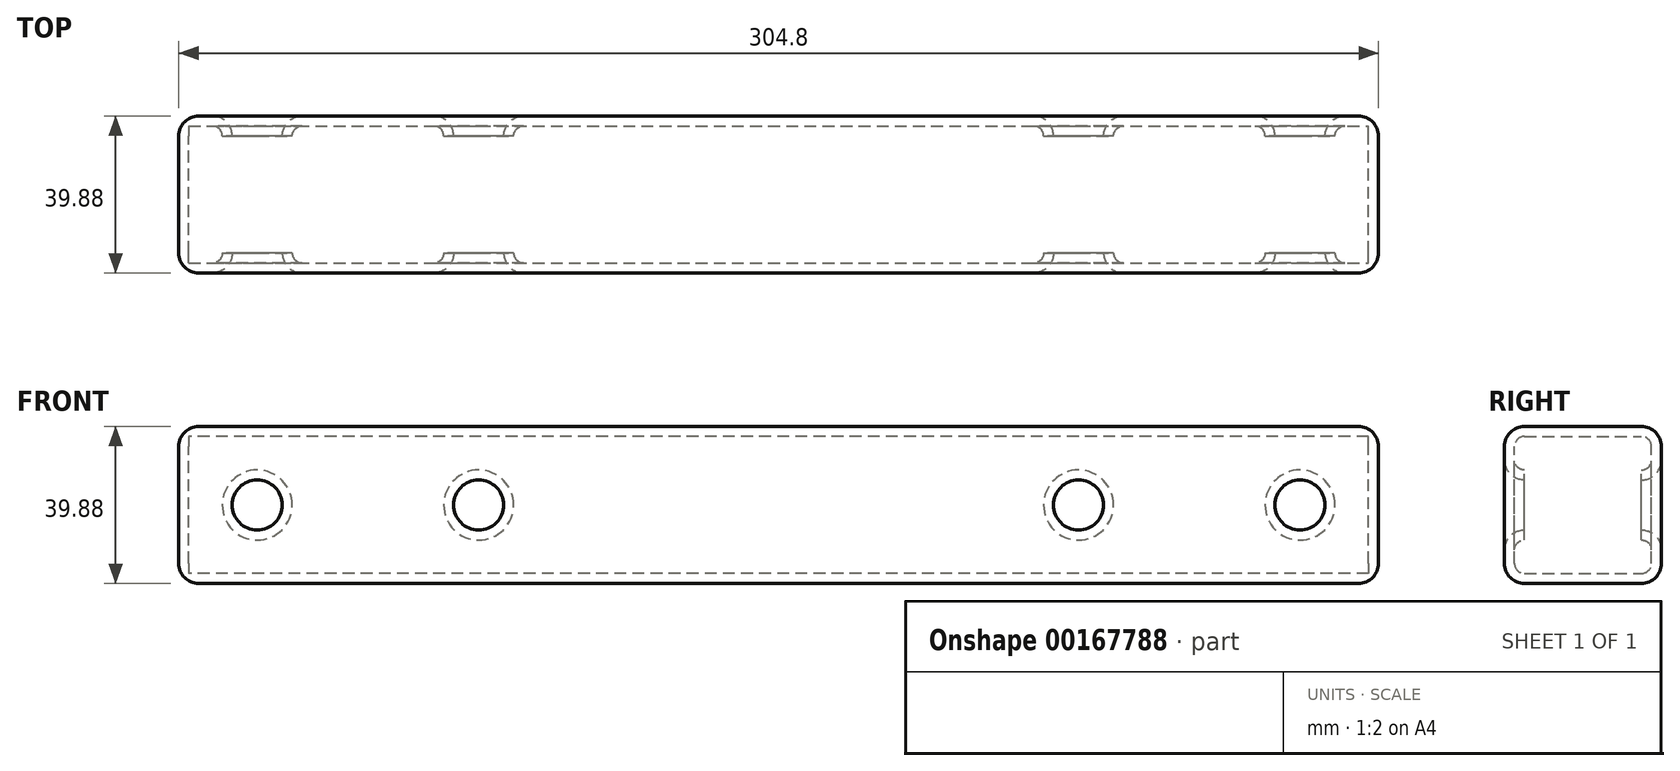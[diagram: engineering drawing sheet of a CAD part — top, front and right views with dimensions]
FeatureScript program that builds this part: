
annotation { "Feature Type Name" : "Feature", "Feature Type Description" : "" }
export const myFeature = defineFeature(function(context is Context, id is Id, definition is map)
    precondition{}
    {
        {
            var Q0;
            Q0=qCreatedBy(makeId("Front.planeOp"),FACE);
            var sketch = newSketch(context, id + "F0", { "sketchPlane" : qUnion([Q0])});
            skLineSegment(sketch, "E0.bottom", {"start": v(152.4, -19.94) * mm, "end": v(-152.4, -19.94) * mm});
            skLineSegment(sketch, "E0.top", {"start": v(152.4, 19.94) * mm, "end": v(-152.4, 19.94) * mm});
            skLineSegment(sketch, "E0.left", {"start": v(152.4, -19.94) * mm, "end": v(152.4, 19.94) * mm});
            skLineSegment(sketch, "E0.right", {"start": v(-152.4, -19.94) * mm, "end": v(-152.4, 19.94) * mm});
            skPoint(sketch, "E0.middle", {"position": v(0, 0) * mm});
            skLineSegment(sketch, "E1", {"start": v(-152.4, 19.94) * mm, "end": v(-112.52, 19.94) * mm});
            skLineSegment(sketch, "E2", {"start": v(-112.52, -19.94) * mm, "end": v(-152.4, -19.94) * mm});
            skPoint(sketch, "E3.startSnap0", {"position": v(-132.46, 19.94) * mm});
            skCircle(sketch, "E4", {"center": v(-132.46, 0) * mm, "radius": 6.35 * mm});
            skCircle(sketch, "E5.MirrorC", {"center": v(132.46, 0) * mm, "radius": 6.35 * mm});
            skLineSegment(sketch, "E6", {"start": v(0, 19.94) * mm, "end": v(-76.2, 19.94) * mm});
            skLineSegment(sketch, "E7", {"start": v(0, 19.94) * mm, "end": v(76.2, 19.94) * mm});
            skCircle(sketch, "E8", {"center": v(-76.2, 0) * mm, "radius": 6.35 * mm});
            skCircle(sketch, "E9.MirrorC", {"center": v(76.2, 0) * mm, "radius": 6.35 * mm});
            skSolve(sketch);
        }
        {
            var Q0;
            Q0=qSketchRegion(id+"F0",true);
            extrude(context, id + "F1", {"entities" : qUnion([Q0]), "depth" : 39.88 * mm});
        }
        {
            var Q0;
            Q0=makeQuery(id+"F1.opExtrude","CAP_EDGE",EDGE,{"disambiguationData":[OSD([sQuery(id+"F0.wireOp",EDGE,"E4")])],"isStart":false});
            var Q1;
            Q1=makeQuery(id+"F1.opExtrude","CAP_EDGE",EDGE,{"disambiguationData":[OSD([sQuery(id+"F0.wireOp",EDGE,"E8")])],"isStart":false});
            var Q2;
            Q2=makeQuery(id+"F1.opExtrude","CAP_EDGE",EDGE,{"disambiguationData":[OSD([sQuery(id+"F0.wireOp",EDGE,"E9.MirrorC")])],"isStart":false});
            fillet(context, id + "F2", {"entities" : qUnion([Q0, Q1, Q2]), "radius" : 5.08 * mm, "tangentPropagation" : true, "allowEdgeOverflow" : false});
        }
        {
            var Q0;
            Q0=makeQuery(id+"F1.opExtrude","CAP_EDGE",EDGE,{"disambiguationData":[OSD([sQuery(id+"F0.wireOp",EDGE,"E5.MirrorC")])],"isStart":false});
            var Q1;
            Q1=makeQuery(id+"F1.opExtrude","CAP_EDGE",EDGE,{"disambiguationData":[OSD([sQuery(id+"F0.wireOp",EDGE,"E5.MirrorC")])],"isStart":true});
            var Q2;
            Q2=makeQuery(id+"F1.opExtrude","CAP_EDGE",EDGE,{"disambiguationData":[OSD([sQuery(id+"F0.wireOp",EDGE,"E9.MirrorC")])],"isStart":true});
            var Q3;
            Q3=makeQuery(id+"F1.opExtrude","CAP_EDGE",EDGE,{"disambiguationData":[OSD([sQuery(id+"F0.wireOp",EDGE,"E8")])],"isStart":true});
            var Q4;
            Q4=makeQuery(id+"F1.opExtrude","CAP_EDGE",EDGE,{"disambiguationData":[OSD([sQuery(id+"F0.wireOp",EDGE,"E4")])],"isStart":true});
            var Q5;
            Q5=makeQuery(id+"F1.opExtrude","CAP_EDGE",EDGE,{"disambiguationData":[OSD([sQuery(id+"F0.wireOp",EDGE,"E0.bottom"),sQuery(id+"F0.wireOp",EDGE,"E2")])],"isStart":true});
            var Q6;
            Q6=makeQuery(id+"F1.opExtrude","CAP_EDGE",EDGE,{"disambiguationData":[OSD([sQuery(id+"F0.wireOp",EDGE,"E0.top"),sQuery(id+"F0.wireOp",EDGE,"E1"),sQuery(id+"F0.wireOp",EDGE,"E6"),sQuery(id+"F0.wireOp",EDGE,"E7")])],"isStart":true});
            var Q7;
            Q7=makeQuery(id+"F1.opExtrude","CAP_EDGE",EDGE,{"disambiguationData":[OSD([sQuery(id+"F0.wireOp",EDGE,"E0.top"),sQuery(id+"F0.wireOp",EDGE,"E1"),sQuery(id+"F0.wireOp",EDGE,"E6"),sQuery(id+"F0.wireOp",EDGE,"E7")])],"isStart":false});
            var Q8;
            Q8=makeQuery(id+"F1.opExtrude","CAP_EDGE",EDGE,{"disambiguationData":[OSD([sQuery(id+"F0.wireOp",EDGE,"E0.bottom"),sQuery(id+"F0.wireOp",EDGE,"E2")])],"isStart":false});
            fillet(context, id + "F3", {"entities" : qUnion([Q0, Q1, Q2, Q3, Q4, Q5, Q6, Q7, Q8]), "radius" : 5.08 * mm, "tangentPropagation" : true, "allowEdgeOverflow" : false});
        }
        {
            var Q0;
            Q0=makeQuery(id+"F1.opExtrude","SWEPT_FACE",FACE,{"disambiguationData":[OSD([sQuery(id+"F0.wireOp",EDGE,"E9.MirrorC")])]});
            var Q1;
            Q1=makeQuery(id+"F1.opExtrude","SWEPT_FACE",FACE,{"disambiguationData":[OSD([sQuery(id+"F0.wireOp",EDGE,"E5.MirrorC")])]});
            var Q2;
            Q2=makeQuery(id+"F1.opExtrude","SWEPT_FACE",FACE,{"disambiguationData":[OSD([sQuery(id+"F0.wireOp",EDGE,"E8")])]});
            var Q3;
            Q3=makeQuery(id+"F1.opExtrude","SWEPT_FACE",FACE,{"disambiguationData":[OSD([sQuery(id+"F0.wireOp",EDGE,"E4")])]});
            shell(context, id + "F4", {"entities" : qUnion([Q0, Q1, Q2, Q3]), "thickness" : 2.54 * mm});
        }
        {
            var Q0;
            Q0=makeQuery(id+"F1.opExtrude","SWEPT_EDGE",EDGE,{"disambiguationData":[OSD([sQuery(id+"F0.wireOp",EDGE,"E0.right"),sQuery(id+"F0.wireOp",EDGE,"E1")])]});
            var Q1;
            Q1=makeQuery(id+"F1.opExtrude","SWEPT_FACE",FACE,{"disambiguationData":[OSD([sQuery(id+"F0.wireOp",EDGE,"E0.left")])]});
            fillet(context, id + "F5", {"entities" : qUnion([Q0, Q1]), "radius" : 5.08 * mm, "tangentPropagation" : true, "allowEdgeOverflow" : false});
        }
    });
